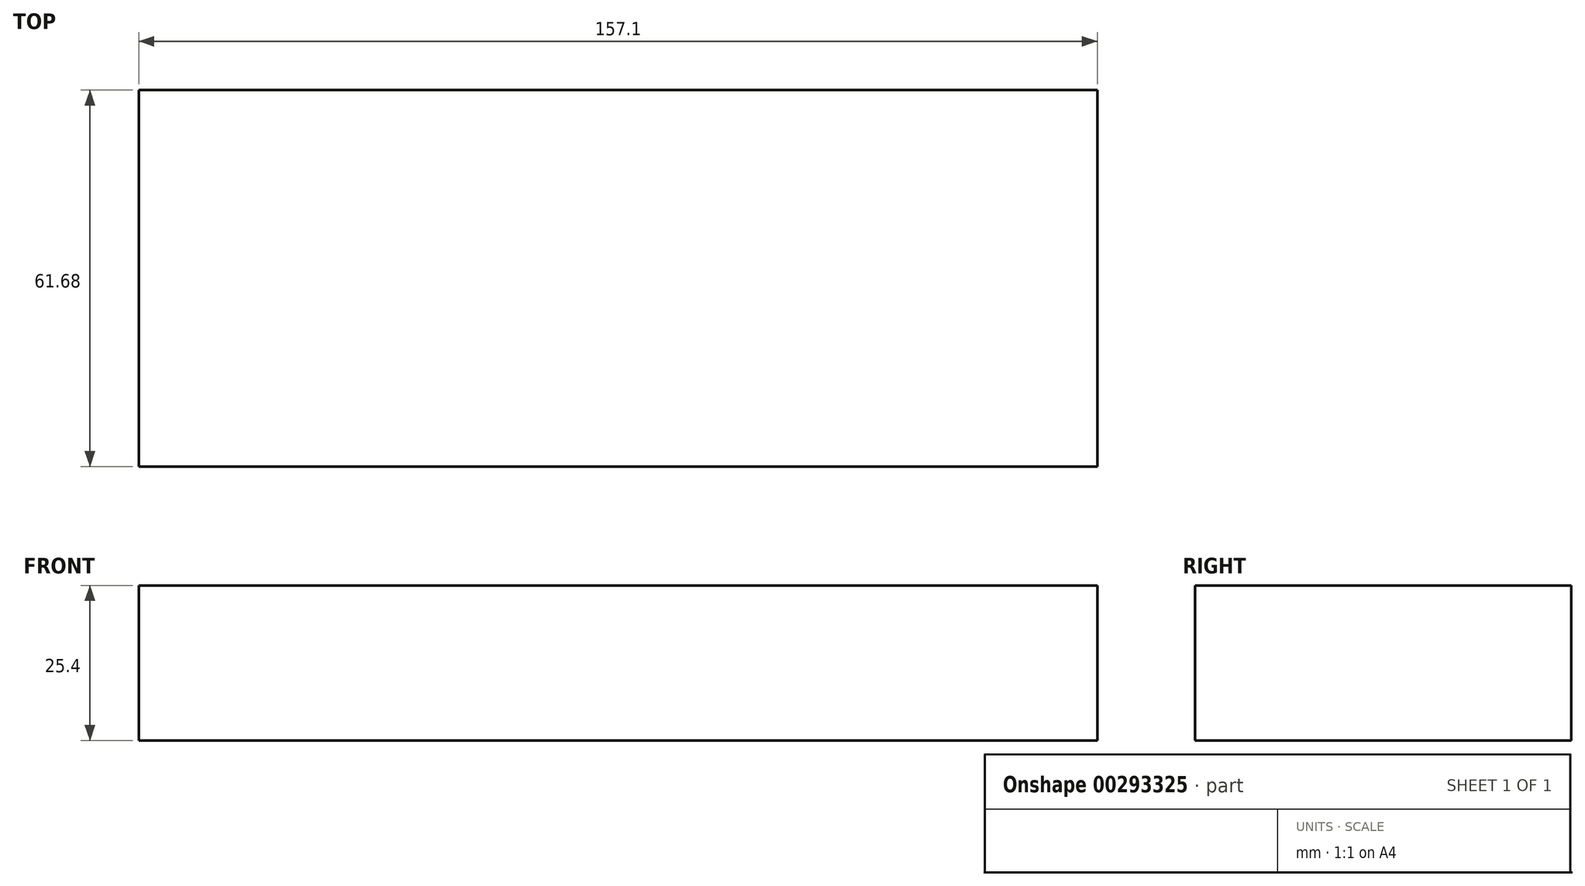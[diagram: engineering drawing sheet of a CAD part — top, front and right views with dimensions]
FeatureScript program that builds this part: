
annotation { "Feature Type Name" : "Feature", "Feature Type Description" : "" }
export const myFeature = defineFeature(function(context is Context, id is Id, definition is map)
    precondition{}
    {
        {
            var Q0;
            Q0=qCreatedBy(makeId("Top.planeOp"),FACE);
            var sketch = newSketch(context, id + "F0", { "sketchPlane" : qUnion([Q0])});
            skLineSegment(sketch, "E0.bottom", {"start": v(-69.96, 14.18) * mm, "end": v(87.14, 14.18) * mm});
            skLineSegment(sketch, "E0.top", {"start": v(-69.96, -47.5) * mm, "end": v(87.14, -47.5) * mm});
            skLineSegment(sketch, "E0.left", {"start": v(-69.96, 14.18) * mm, "end": v(-69.96, -47.5) * mm});
            skLineSegment(sketch, "E0.right", {"start": v(87.14, 14.18) * mm, "end": v(87.14, -47.5) * mm});
            skSolve(sketch);
        }
        {
            var Q0;
            Q0=makeQuery(id+"F0.imprint","IMPRINT",FACE,{"disambiguationData":[TD([[makeQuery(id+"F0.imprint","IMPRINT",EDGE,{"derivedFrom":sQuery(id+"F0.wireOp",EDGE,"E0.bottom")}),-1.0]])]});
            extrude(context, id + "F1", {"entities" : qUnion([Q0]), "depth" : 25.4 * mm});
        }
    });
